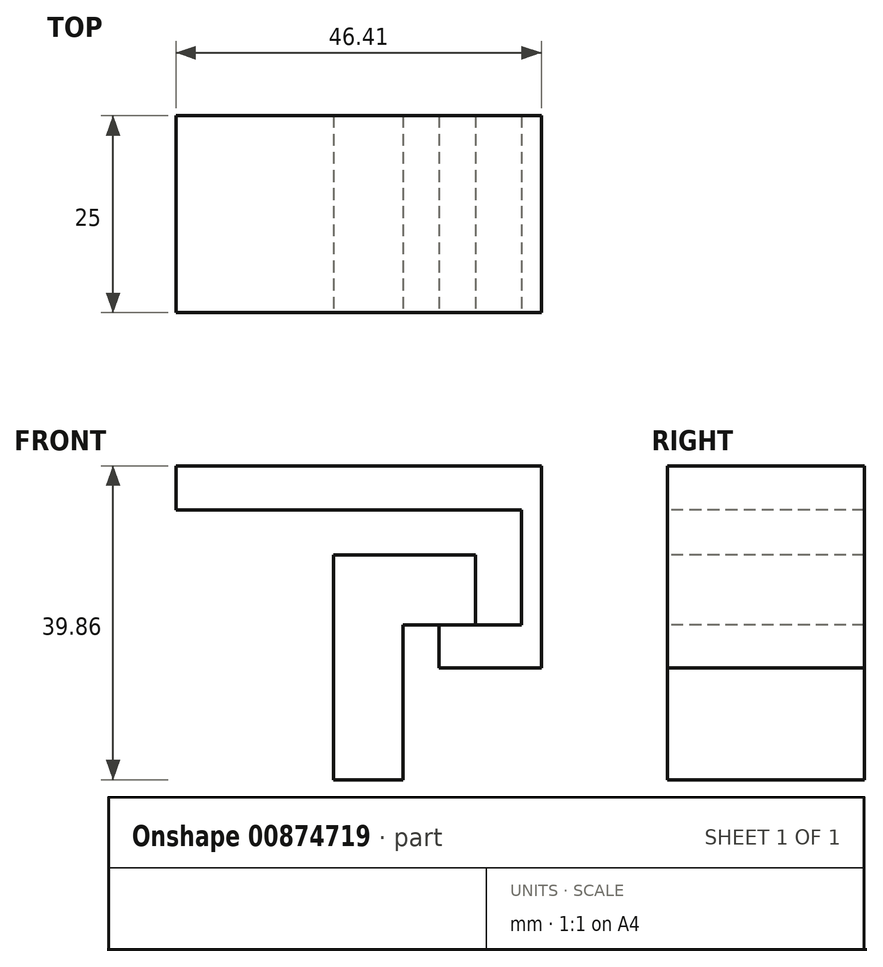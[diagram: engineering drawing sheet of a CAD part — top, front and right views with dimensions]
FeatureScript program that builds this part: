
annotation { "Feature Type Name" : "Feature", "Feature Type Description" : "" }
export const myFeature = defineFeature(function(context is Context, id is Id, definition is map)
    precondition{}
    {
        {
            var Q0;
            Q0=qCreatedBy(makeId("Front.planeOp"),FACE);
            var sketch = newSketch(context, id + "F0", { "sketchPlane" : qUnion([Q0])});
            skLineSegment(sketch, "E0", {"start": v(0, 28.55) * mm, "end": v(0, 0) * mm});
            skLineSegment(sketch, "E1", {"start": v(0, 28.55) * mm, "end": v(18.03, 28.55) * mm});
            skLineSegment(sketch, "E2", {"start": v(18.03, 28.55) * mm, "end": v(18.03, 19.64) * mm});
            skLineSegment(sketch, "E3", {"start": v(18.03, 19.64) * mm, "end": v(8.83, 19.64) * mm});
            skLineSegment(sketch, "E4", {"start": v(8.83, 19.64) * mm, "end": v(8.83, 0) * mm});
            skLineSegment(sketch, "E5", {"start": v(8.83, 0) * mm, "end": v(0, 0) * mm});
            skSolve(sketch);
        }
        {
            var Q0;
            Q0 = qSketchRegion(id + "F0", true);
            extrude(context, id + "F1", {"entities" : qUnion([Q0]), "oppositeDirection" : true, "depth" : 25 * mm, "offsetDistance" : 25 * mm});
        }
        {
            var Q0;
            Q0=makeQuery(id+"F1.opExtrude","CAP_FACE",FACE,{"disambiguationData":[OSD([sQuery(id+"F0.wireOp",EDGE,"E0"),sQuery(id+"F0.wireOp",EDGE,"E1"),sQuery(id+"F0.wireOp",EDGE,"E2"),sQuery(id+"F0.wireOp",EDGE,"E3"),sQuery(id+"F0.wireOp",EDGE,"E4"),sQuery(id+"F0.wireOp",EDGE,"E5")])],"isStart":true});
            var sketch = newSketch(context, id + "F2", { "sketchPlane" : qUnion([Q0])});
            skLineSegment(sketch, "E6", {"start": v(13.43, 19.64) * mm, "end": v(26.42, 19.64) * mm});
            skLineSegment(sketch, "E7", {"start": v(26.42, 19.64) * mm, "end": v(26.42, 39.86) * mm});
            skLineSegment(sketch, "E8", {"start": v(26.42, 39.86) * mm, "end": v(-20, 39.86) * mm});
            skLineSegment(sketch, "E9", {"start": v(-20, 39.86) * mm, "end": v(-20, 34.29) * mm});
            skLineSegment(sketch, "E10", {"start": v(-20, 34.29) * mm, "end": v(23.86, 34.29) * mm});
            skLineSegment(sketch, "E11", {"start": v(23.86, 34.29) * mm, "end": v(23.86, 19.64) * mm});
            skLineSegment(sketch, "E12", {"start": v(13.43, 19.64) * mm, "end": v(13.43, 14.2) * mm});
            skLineSegment(sketch, "E13", {"start": v(13.43, 14.2) * mm, "end": v(26.42, 14.2) * mm});
            skLineSegment(sketch, "E14", {"start": v(26.42, 14.2) * mm, "end": v(26.42, 19.64) * mm});
            skSolve(sketch);
        }
        {
            var Q0;
            Q0 = qSketchRegion(id + "F2", true);
            extrude(context, id + "F3", {"entities" : qUnion([Q0]), "oppositeDirection" : true, "depth" : 25 * mm, "offsetDistance" : 25 * mm});
        }
    });
